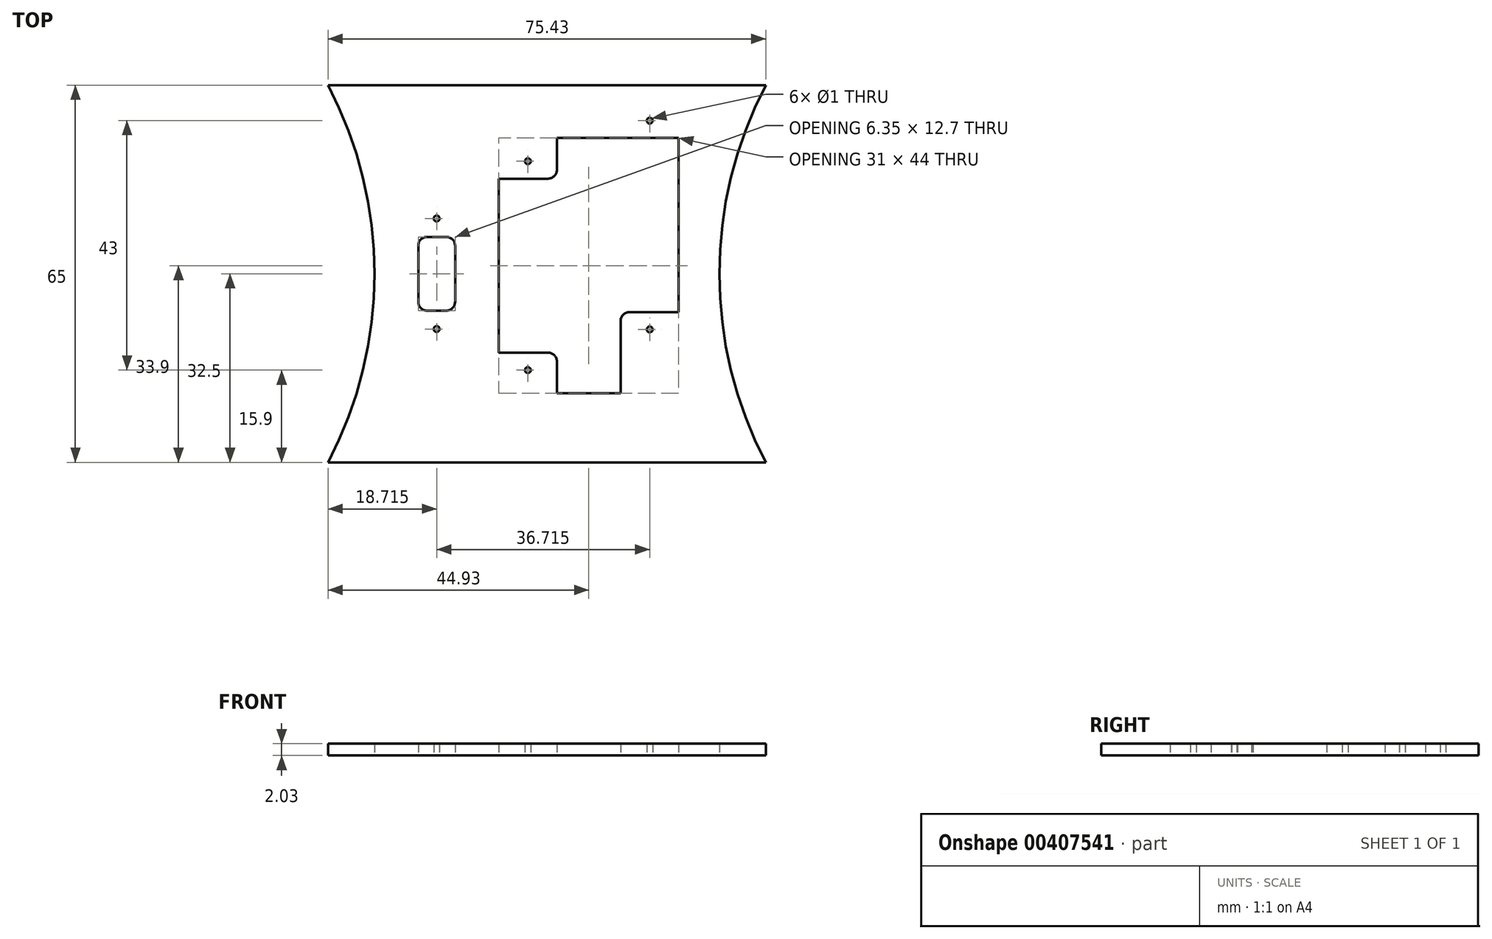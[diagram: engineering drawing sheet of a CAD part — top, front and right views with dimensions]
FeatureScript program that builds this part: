
annotation { "Feature Type Name" : "Feature", "Feature Type Description" : "" }
export const myFeature = defineFeature(function(context is Context, id is Id, definition is map)
    precondition{}
    {
        {
            var Q0;
            Q0=qCreatedBy(makeId("Top.planeOp"),FACE);
            var sketch = newSketch(context, id + "F0", { "sketchPlane" : qUnion([Q0])});
            skCircle(sketch, "E0", {"center": v(10.71, -9.53) * mm, "radius": 0.5 * mm});
            skCircle(sketch, "E1.1.0.0", {"center": v(10.71, 9.52) * mm, "radius": 0.5 * mm});
            skPoint(sketch, "E2.middle", {"position": v(10.71, 0) * mm});
            skLineSegment(sketch, "E3.bottom", {"start": v(16.43, 12.06) * mm, "end": v(16.43, -12.07) * mm, "construction": true});
            skLineSegment(sketch, "E3.top", {"start": v(5, 12.06) * mm, "end": v(5, -12.07) * mm, "construction": true});
            skLineSegment(sketch, "E3.left", {"start": v(16.43, 12.07) * mm, "end": v(5, 12.07) * mm, "construction": true});
            skLineSegment(sketch, "E3.right", {"start": v(16.43, -12.06) * mm, "end": v(5, -12.07) * mm, "construction": true});
            skLineSegment(sketch, "E4.bottom", {"start": v(13.89, -4.85) * mm, "end": v(13.89, 4.85) * mm});
            skLineSegment(sketch, "E4.top", {"start": v(7.54, -4.85) * mm, "end": v(7.54, 4.85) * mm});
            skLineSegment(sketch, "E4.left", {"start": v(12.39, -6.35) * mm, "end": v(9.04, -6.35) * mm});
            skLineSegment(sketch, "E4.right", {"start": v(12.39, 6.35) * mm, "end": v(9.04, 6.35) * mm});
            skLineSegment(sketch, "E5", {"start": v(13.89, 0) * mm, "end": v(7.54, 0) * mm, "construction": true});
            skLineSegment(sketch, "E6", {"start": v(10.71, 9.52) * mm, "end": v(10.71, -9.53) * mm, "construction": true});
            skArc(sketch, "E7.filletArc", {"start": v(13.89, 4.85) * mm, "mid": v(13.45, 5.91) * mm, "end": v(12.39, 6.35) * mm});
            skPoint(sketch, "E8.visualSharp", {"position": v(7.54, 6.35) * mm});
            skArc(sketch, "E8.filletArc", {"start": v(9.04, 6.35) * mm, "mid": v(7.98, 5.91) * mm, "end": v(7.54, 4.85) * mm});
            skPoint(sketch, "E9.visualSharp", {"position": v(7.54, -6.35) * mm});
            skArc(sketch, "E9.filletArc", {"start": v(7.54, -4.85) * mm, "mid": v(7.98, -5.91) * mm, "end": v(9.04, -6.35) * mm});
            skPoint(sketch, "E10.visualSharp", {"position": v(13.89, -6.35) * mm});
            skArc(sketch, "E10.filletArc", {"start": v(12.39, -6.35) * mm, "mid": v(13.45, -5.91) * mm, "end": v(13.89, -4.85) * mm});
            skCircle(sketch, "E11", {"center": v(47.43, 26.4) * mm, "radius": 0.5 * mm});
            skCircle(sketch, "E12.MirrorC", {"center": v(47.43, -9.6) * mm, "radius": 0.5 * mm});
            skLineSegment(sketch, "E13.MirrorCS", {"start": v(52.43, -6.6) * mm, "end": v(43.93, -6.6) * mm});
            skLineSegment(sketch, "E14", {"start": v(0, 0) * mm, "end": v(59.43, 0) * mm, "construction": true});
            skLineSegment(sketch, "E15.MirrorCS", {"start": v(29.93, 16.4) * mm, "end": v(21.43, 16.4) * mm});
            skPoint(sketch, "E16.MirrorP", {"position": v(26.43, 19.4) * mm});
            skPoint(sketch, "E17.MirrorP", {"position": v(26.43, -16.6) * mm});
            skLineSegment(sketch, "E18.MirrorCS", {"start": v(21.43, -13.6) * mm, "end": v(29.93, -13.6) * mm});
            skCircle(sketch, "E19.MirrorC", {"center": v(26.43, -7) * mm, "radius": 2.5 * mm, "construction": true});
            skLineSegment(sketch, "E20", {"start": v(31.43, 23.4) * mm, "end": v(31.43, 17.9) * mm});
            skLineSegment(sketch, "E21", {"start": v(21.43, 16.4) * mm, "end": v(21.43, -13.6) * mm});
            skLineSegment(sketch, "E22", {"start": v(52.43, 23.4) * mm, "end": v(52.43, -6.6) * mm});
            skPoint(sketch, "E23.visualSharp", {"position": v(31.43, 16.4) * mm});
            skArc(sketch, "E23.filletArc", {"start": v(29.93, 16.4) * mm, "mid": v(31, 16.84) * mm, "end": v(31.43, 17.9) * mm});
            skPoint(sketch, "E24.orphan", {"position": v(59.43, 0) * mm});
            skLineSegment(sketch, "E25", {"start": v(0, 0) * mm, "end": v(0, 32.5) * mm, "construction": true});
            skLineSegment(sketch, "E26.MirrorCS", {"start": v(0, 0) * mm, "end": v(0, -32.5) * mm, "construction": true});
            skCircle(sketch, "E27", {"center": v(26.43, -16.6) * mm, "radius": 0.5 * mm});
            skCircle(sketch, "E28", {"center": v(26.43, 19.4) * mm, "radius": 0.5 * mm});
            skLineSegment(sketch, "E29", {"start": v(31.43, -20.6) * mm, "end": v(31.43, -15.1) * mm});
            skArc(sketch, "E30.filletArc", {"start": v(31.43, -15.1) * mm, "mid": v(31, -14.04) * mm, "end": v(29.93, -13.6) * mm});
            skArc(sketch, "E31", {"start": v(-8, -32.5) * mm, "mid": v(0, 0) * mm, "end": v(-8, 32.5) * mm});
            skLineSegment(sketch, "E32", {"start": v(-8, -32.5) * mm, "end": v(67.43, -32.5) * mm});
            skLineSegment(sketch, "E33", {"start": v(59.43, -32.5) * mm, "end": v(59.43, 32.5) * mm, "construction": true});
            skLineSegment(sketch, "E34", {"start": v(-8, 32.5) * mm, "end": v(67.43, 32.5) * mm});
            skPoint(sketch, "E35", {"position": v(10.71, -12.07) * mm});
            skArc(sketch, "E36", {"start": v(67.43, 32.5) * mm, "mid": v(59.43, 0) * mm, "end": v(67.43, -32.5) * mm});
            skLineSegment(sketch, "E37", {"start": v(31.43, -20.6) * mm, "end": v(42.43, -20.6) * mm});
            skLineSegment(sketch, "E38", {"start": v(31.43, 23.4) * mm, "end": v(52.43, 23.4) * mm});
            skLineSegment(sketch, "E39", {"start": v(42.43, -20.6) * mm, "end": v(42.43, -8.1) * mm});
            skPoint(sketch, "E40.visualSharp", {"position": v(42.43, -6.6) * mm});
            skArc(sketch, "E40.filletArc", {"start": v(43.93, -6.6) * mm, "mid": v(42.87, -7.04) * mm, "end": v(42.43, -8.1) * mm});
            skLineSegment(sketch, "E41", {"start": v(52.43, 8.4) * mm, "end": v(21.43, 8.4) * mm, "construction": true});
            skCircle(sketch, "E42", {"center": v(47.43, 0) * mm, "radius": 2.5 * mm, "construction": true});
            skSolve(sketch);
        }
        {
            var Q0;
            Q0=makeQuery(id+"F0.imprint","IMPRINT",FACE,{"disambiguationData":[TD([[makeQuery(id+"F0.imprint","IMPRINT",EDGE,{"derivedFrom":sQuery(id+"F0.wireOp",EDGE,"E0")}),-1.0]])]});
            extrude(context, id + "F1", {"entities" : qUnion([Q0]), "depth" : 2.03 * mm});
        }
    });
